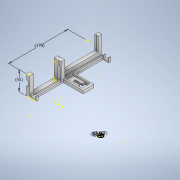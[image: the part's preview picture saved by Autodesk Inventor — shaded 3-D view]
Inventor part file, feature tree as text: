
AUTODESK INVENTOR PART (.ipt)
format: ipt  version: 2020 (Build 240168000, 168)  size: 1,139,712 bytes
history: native  units: mm
features: sketch x87, extrude x63, pattern_circular x1, pattern_linear x1
ambient origin geometry x8: Origin, YZ Plane, XZ Plane, XY Plane, X Axis, Y Axis, Z Axis, Center Point
bodies: Solid1 (feature_tree)
feature tree (152):
  extrude  "Extrusion1"  Depth=200.0mm
  extrude  "Extrusion2"  Depth=100.0mm
  extrude  "Extrusion3"  Depth=20.0mm
  extrude  "Extrusion4"  Depth=10.0mm
  extrude  "Extrusion5"  Depth=100.0mm
  extrude  "Extrusion6"  Depth=10.0mm
  extrude  "Extrusion7"  Depth=10.0mm TaperAngle=0.0deg
  extrude  "Extrusion8"  Depth=50.0mm TaperAngle=0.0deg
  extrude  "Extrusion9"  Depth=10.0mm TaperAngle=0.0deg
  extrude  "Extrusion10"  Depth=3.0mm
  extrude  "Extrusion11"  Depth=1.5mm
  sketch  "Sketch14"  dims[d28=1.0mm d29=1.0mm]
  extrude  "Extrusion12"  Depth=1.0mm
  extrude  "Extrusion13"  Depth=1.5mm
  extrude  "Extrusion14"  Depth=5.0mm TaperAngle=0.0deg
  extrude  "Extrusion15"  Depth=5.0mm TaperAngle=0.0deg
  sketch  "Sketch19"  dims[d45=5.0mm d46=0.0mm d47=70.0mm]
  extrude  "Extrusion16"  Depth=5.0mm TaperAngle=0.0deg
  sketch  "Sketch21"  dims[d51=80.75mm d52=0.0mm d53=10.0mm d54=0.0mm]
  extrude  "Extrusion17"  Depth=70.0mm
  extrude  "Extrusion18"  Depth=5.0mm TaperAngle=0.0deg
  extrude  "Extrusion19"  Depth=10.0mm TaperAngle=0.0deg
  extrude  "Extrusion20"  Depth=10.0mm TaperAngle=0.0deg
  extrude  "Extrusion21"  Depth=40.0mm
  extrude  "Extrusion24"  Depth=88.0mm TaperAngle=0.0deg
  extrude  "Extrusion25"  Depth=8.0mm
  extrude  "Extrusion26"  Depth=3.0mm
  extrude  "Extrusion27"  Depth=72.0mm TaperAngle=0.0deg
  extrude  "Extrusion28"  Depth=1.5mm
  extrude  "Extrusion29"  Depth=1.5mm TaperAngle=0.0deg
  extrude  "Extrusion30"  Depth=6.0mm
  extrude  "Extrusion31"  Depth=1.0mm
  extrude  "Extrusion32"  Depth=1.0mm
  extrude  "Extrusion33"  Depth=6.0mm
  pattern_circular  "Circular Pattern1"  Count=21 Angle=360.0deg
  extrude  "Extrusion34"  Depth=26.0mm TaperAngle=0.0deg
  extrude  "Extrusion35"  Depth=8.0mm
  sketch  "Sketch44"  dims[d102=1.0mm]
  extrude  "Extrusion36"  Depth=8.0mm
  extrude  "Extrusion37"  Depth=45.0mm TaperAngle=0.0deg
  extrude  "Extrusion40"  Depth=8.0mm
  extrude  "Extrusion41"  Depth=30.5mm TaperAngle=0.0deg
  extrude  "Extrusion42"  Depth=23.0mm
  extrude  "Extrusion43"  Depth=30.5mm TaperAngle=0.0deg
  extrude  "Extrusion44"  Depth=4.0mm
  extrude  "Extrusion45"  Depth=4.0mm TaperAngle=0.0deg
  extrude  "Extrusion46"  Depth=10.0mm TaperAngle=0.0deg
  sketch  "Sketch58"  dims[d116=1.0mm]
  sketch  "Sketch59"  dims[d117=2.0mm]
  sketch  "Sketch60"  dims[d118=4.3mm]
  extrude  "Extrusion47"  Depth=8.0mm
  extrude  "Extrusion48"  Depth=2.0mm TaperAngle=0.0deg
  pattern_linear  "Rectangular Pattern1"  Count1=55 Spacing1=2.0mm
  extrude  "Extrusion49"  Depth=4.0mm TaperAngle=0.0deg
  sketch  "Sketch64"  dims[d123=10.1mm]
  extrude  "Extrusion50"  Depth=55.0mm
  sketch  "Sketch66"  dims[d133=24.5mm d134=0.0mm]
  sketch  "Sketch67"  dims[d135=1.0mm]
  extrude  "Extrusion51"  TaperAngle=150.0deg  [1 undecoded]
  sketch  "Sketch69"  dims[d137=22.68928mm]
  sketch  "Sketch70"  dims[d138=26.0mm d139=0.0mm d140=210.0mm d141=360.0deg]
  sketch  "Sketch71"  dims[d143=24.5mm d144=0.0mm d145=26.0mm d146=0.0mm]
  sketch  "Sketch72"  dims[d147=8.0mm d148=8.0mm]
  sketch  "Sketch73"  dims[d149=8.0mm d150=8.0mm]
  sketch  "Sketch74"  dims[d151=4.5mm d152=0.0mm d153=45.0mm d154=0.0mm]
  extrude  "Extrusion52"  Depth=12.5mm TaperAngle=0.0deg
  extrude  "Extrusion53"  Depth=2.0mm
  extrude  "Extrusion54"  Depth=6.0mm TaperAngle=0.0deg
  extrude  "Extrusion55"  Depth=6.0mm TaperAngle=0.0deg
  extrude  "Extrusion56"  Depth=11.5mm TaperAngle=0.0deg
  sketch  "Sketch80"  dims[d172=4.0mm d173=4.0mm d174=0.0mm]
  extrude  "Extrusion57"  Depth=15.0mm
  extrude  "Extrusion58"  Depth=5.0mm TaperAngle=0.0deg
  extrude  "Extrusion59"  Depth=4.0mm
  extrude  "Extrusion60"  Depth=2.0mm
  extrude  "Extrusion61"  Depth=2.0mm
  extrude  "Extrusion62"  Depth=5.0mm TaperAngle=0.0deg
  extrude  "Extrusion63"  Depth=3.0mm
  extrude  "Extrusion64"  Depth=6.0mm TaperAngle=0.0deg
  sketch  "Sketch89"  dims[d190=4.0mm]
  extrude  "Extrusion65"  Depth=3.0mm
  extrude  "Extrusion66"  Depth=6.0mm TaperAngle=0.0deg
  extrude  "Extrusion67"  Depth=6.0mm TaperAngle=0.0deg
  sketch  "Sketch93"  dims[d195=2.0mm]
  sketch  "Sketch94"  dims[d206=0.5mm]
  sketch  "Sketch95"  dims[d209=0.5mm]
  sketch  "Sketch96"  dims[d210=2.0mm d211=0.0mm d212=550.0mm d214=2.0mm]
  sketch  "Sketch97"  dims[d215=4.0mm d216=0.0mm d217=4.0mm d218=0.0mm]
  sketch  "Sketch98"  dims[d219=170.0mm d220=55.0mm d221=150.0deg d222=12.5mm d223=0.0mm d224=2.0mm d225=138.0mm d226=0.0mm d227=2.25mm d228=0.0mm d229=11.5mm d230=0.0mm d231=15.0mm d232=5.0mm d233=0.0mm d234=4.0mm d235=2.0mm d236=2.0mm d237=5.0mm d238=0.0mm d239=3.0mm d240=339.0mm d241=0.0mm d242=3.0mm d243=339.0mm d244=0.0mm d245=339.0mm d246=0.0mm d247=36.0mm d248=0.0mm d249=0.25mm d250=0.25mm d251=15.5mm d252=0.0mm d253=10.0mm d254=36.0mm d255=0.2mm d256=0.2mm d257=15.5mm d258=0.0mm d259=27.5mm d260=0.0mm d261=6.75mm d262=0.0mm d263=12.5mm d264=6.75mm d265=0.0mm d266=6.0mm d267=6.75mm d268=0.0mm d269=15.75mm d270=0.0mm]
  sketch  "Sketch1"  dims[d0=200.0mm d1=200.0mm]
  sketch  "Sketch2"  dims[d2=100.0mm d3=100.0mm]
  sketch  "Sketch3"  dims[d4=50.0mm d5=0.0mm d6=20.0mm]
  sketch  "Sketch4"  dims[d7=50.0mm d8=0.0mm d9=10.0mm]
  sketch  "Sketch5"  dims[d10=40.0mm d11=100.0mm]
  sketch  "Sketch6"  dims[d12=10.0mm d13=10.0mm]
  sketch  "Sketch8"  dims[d14=10.0mm d15=34.75mm d16=0.0mm]
  sketch  "Sketch9"  dims[d17=10.0mm d18=50.0mm d19=0.0mm]
  sketch  "Sketch11"  dims[d20=3.0mm d21=10.0mm d22=0.0mm]
  sketch  "Sketch12"  dims[d23=47.0mm d24=0.0mm d25=3.0mm]
  sketch  "Sketch13"  dims[d26=1.5mm d27=1.5mm]
  sketch  "Sketch15"  dims[d30=5.0mm d31=0.0mm d32=1.5mm]
  sketch  "Sketch16"  dims[d33=1.5mm d34=5.0mm d35=0.0mm]
  sketch  "Sketch17"  dims[d38=5.0mm d39=379.25mm d40=0.0mm]
  sketch  "Sketch18"  dims[d41=5.0mm d42=261.5mm d43=0.0mm]
  sketch  "Sketch20"  dims[d48=10.0mm d49=5.0mm d50=0.0mm]
  sketch  "Sketch22"  dims[d55=10.0mm d56=0.0mm d57=194.25mm d58=0.0mm]
  sketch  "Sketch23"  dims[d59=3.5mm d60=40.0mm]
  sketch  "Sketch24"  dims[d61=88.0mm d62=0.0mm d63=88.0mm d64=0.0mm]
  sketch  "Sketch25"  dims[d65=175.25mm d66=0.0mm d67=8.0mm]
  sketch  "Sketch28"  dims[d68=3.5mm d69=3.0mm]
  sketch  "Sketch31"  dims[d70=175.25mm d71=0.0mm d72=72.0mm d73=0.0mm]
  sketch  "Sketch32"  dims[d78=14.25mm d79=0.0mm d80=1.5mm]
  sketch  "Sketch33"  dims[d81=1.5mm d82=246.0mm d83=0.0mm]
  sketch  "Sketch34"  dims[d84=12.5mm d85=6.0mm]
  sketch  "Sketch35"  dims[d86=1.0mm d88=2.1mm]
  sketch  "Sketch36"  dims[d90=4.0mm d91=1.0mm]
  sketch  "Sketch38"  dims[d92=7.0mm d93=0.0mm d94=6.0mm]
  sketch  "Sketch39"  dims[d95=7.0mm d96=0.0mm]
  sketch  "Sketch40"  dims[d97=12.5mm]
  sketch  "Sketch41"  dims[d98=6.0mm]
  sketch  "Sketch42"  dims[d100=2.1mm]
  sketch  "Sketch43"  dims[d101=2.1mm]
  sketch  "Sketch45"  dims[d103=2.0mm]
  sketch  "Sketch46"  dims[d104=1.0mm]
  sketch  "Sketch49"  dims[d105=2.0mm]
  sketch  "Sketch50"  dims[d106=7.0mm d107=0.0mm]
  sketch  "Sketch51"  dims[d108=6.0mm]
  sketch  "Sketch52"  dims[d109=7.0mm d110=0.0mm]
  sketch  "Sketch53"  dims[d113=2.1mm]
  sketch  "Sketch56"  dims[d114=1.0mm]
  sketch  "Sketch57"  dims[d115=2.0mm]
  sketch  "Sketch61"  dims[d119=84.0mm]
  sketch  "Sketch62"  dims[d120=9.25mm d121=0.0mm]
  sketch  "Sketch63"  dims[d122=5.1mm]
  sketch  "Sketch65"  dims[d124=24.5mm d125=0.0mm]
  sketch  "Sketch68"  dims[d136=8.726646mm]
  sketch  "Sketch75"  dims[d159=16.0mm d160=8.0mm]
  sketch  "Sketch76"  dims[d161=8.0mm d162=30.5mm d163=0.0mm]
  sketch  "Sketch77"  dims[d164=10.9mm d165=23.0mm]
  sketch  "Sketch78"  dims[d166=10.0mm d167=30.5mm d168=0.0mm]
  sketch  "Sketch79"  dims[d169=4.0mm d170=0.0mm d171=4.0mm]
  sketch  "Sketch81"  dims[d175=4.0mm d176=0.0mm d177=10.0mm d178=0.0mm]
  sketch  "Sketch82"  dims[d179=6.0mm d180=8.0mm]
  sketch  "Sketch83"  dims[d181=8.0mm d182=2.0mm d183=0.0mm]
  sketch  "Sketch84"  dims[d184=0.5mm]
  sketch  "Sketch85"  dims[d185=16.954627mm]
  sketch  "Sketch86"  dims[d187=0.5mm]
  sketch  "Sketch87"  dims[d188=12.002203mm]
  sketch  "Sketch88"  dims[d189=13.453434mm]
  sketch  "Sketch90"  dims[d191=2.0mm d192=0.0mm]
  sketch  "Sketch91"  dims[d193=1.45mm]
  sketch  "Sketch92"  dims[d194=2.075641mm]
note: 1 required parameter value undecoded (feature->parameter linkage not recoverable at this tier; creation-order binding heuristic only, values carry confidence <= 0.55)
